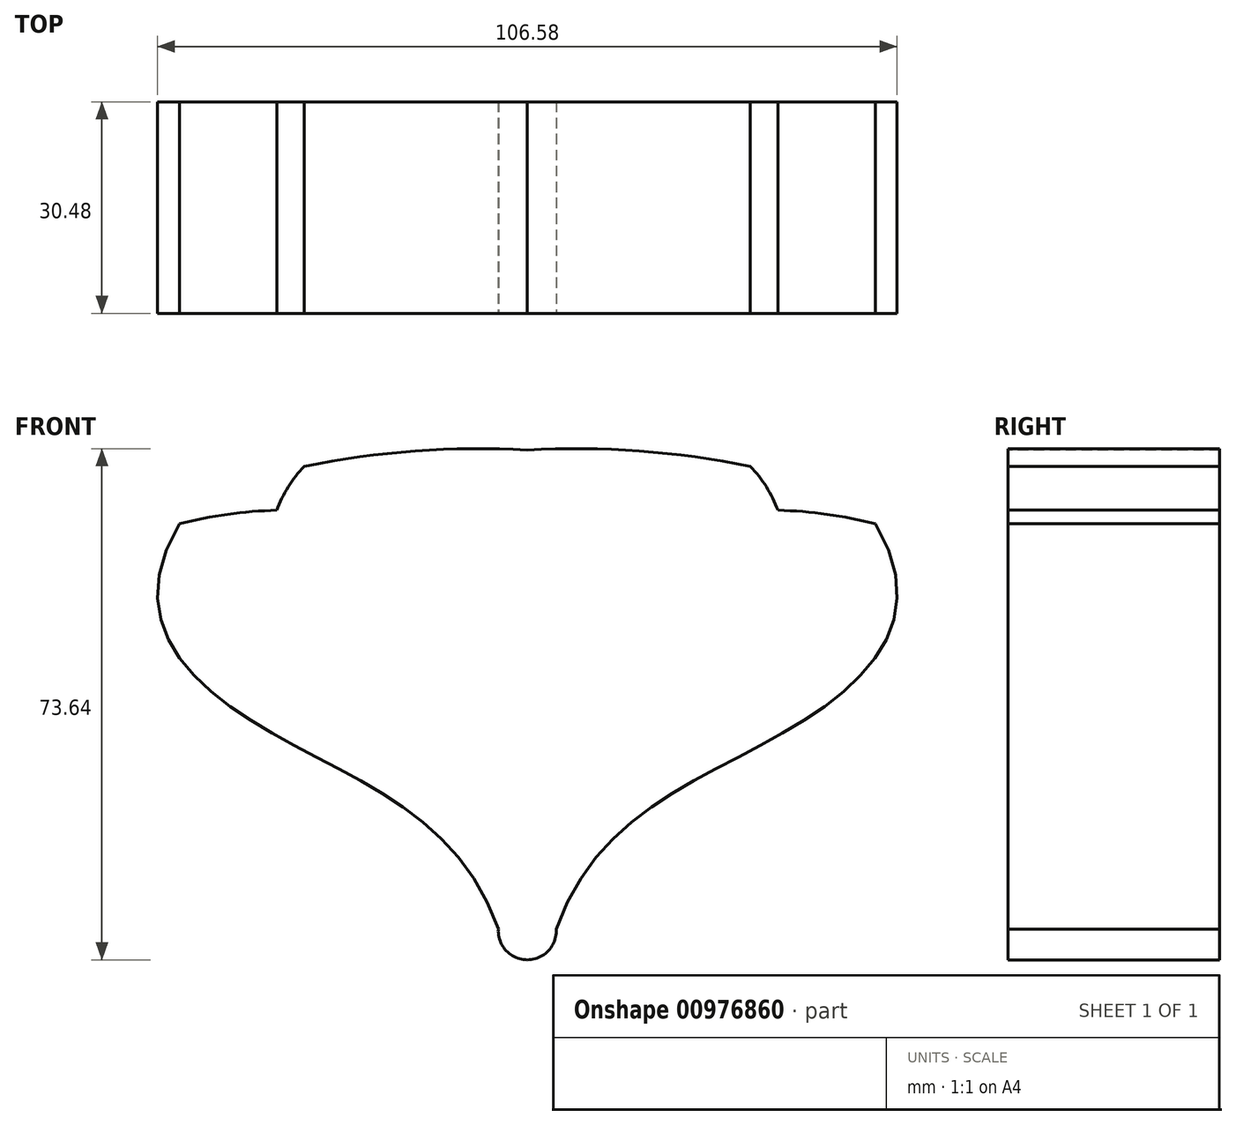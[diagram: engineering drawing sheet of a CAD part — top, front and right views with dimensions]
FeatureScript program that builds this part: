
annotation { "Feature Type Name" : "Feature", "Feature Type Description" : "" }
export const myFeature = defineFeature(function(context is Context, id is Id, definition is map)
    precondition{}
    {
        {
            var Q0;
            Q0=qCreatedBy(makeId("Front.planeOp"),FACE);
            var sketch = newSketch(context, id + "F0", { "sketchPlane" : qUnion([Q0])});
            skLineSegment(sketch, "E0.bottom", {"start": v(50.14, 29.21) * mm, "end": v(-50.14, 29.21) * mm, "construction": true});
            skLineSegment(sketch, "E0.top", {"start": v(50.14, -29.21) * mm, "end": v(-50.14, -29.21) * mm, "construction": true});
            skLineSegment(sketch, "E0.left", {"start": v(50.14, 29.21) * mm, "end": v(50.14, -29.21) * mm, "construction": true});
            skLineSegment(sketch, "E0.right", {"start": v(-50.14, 29.21) * mm, "end": v(-50.14, -29.21) * mm, "construction": true});
            skPoint(sketch, "E0.middle", {"position": v(0, 0) * mm});
            skFitSpline(sketch, "E1", {"points": [v(-50.14, 29.21) * mm, v(-38.39, 0) * mm, v(-4.18, -29.21) * mm], "startDerivative": vector(-53.87, -90.67) * mm, "endDerivative": vector(32.95, -94.62) * mm});
            skPoint(sketch, "E2", {"position": v(-50.14, 0) * mm});
            skFitSpline(sketch, "E3.MirrorCS", {"points": [v(50.14, 29.21) * mm, v(38.39, 0) * mm, v(4.18, -29.21) * mm], "startDerivative": vector(53.87, -90.67) * mm, "endDerivative": vector(-32.95, -94.62) * mm});
            skArc(sketch, "E4", {"start": v(-4.18, -29.21) * mm, "mid": v(0, -33.6) * mm, "end": v(4.18, -29.21) * mm});
            skLineSegment(sketch, "E5.bottom", {"start": v(-50.14, 29.21) * mm, "end": v(-45.63, 29.21) * mm});
            skLineSegment(sketch, "E6.bottom", {"start": v(-50.14, 29.21) * mm, "end": v(50.14, 29.21) * mm, "construction": true});
            skLineSegment(sketch, "E6.top", {"start": v(-50.14, 39.83) * mm, "end": v(50.14, 39.83) * mm, "construction": true});
            skLineSegment(sketch, "E6.left", {"start": v(-50.14, 29.21) * mm, "end": v(-50.14, 39.83) * mm, "construction": true});
            skLineSegment(sketch, "E6.right", {"start": v(50.14, 29.21) * mm, "end": v(50.14, 39.83) * mm, "construction": true});
            skArc(sketch, "E7", {"start": v(0, 39.83) * mm, "mid": v(-16.14, 39.7) * mm, "end": v(-32.13, 37.5) * mm});
            skArc(sketch, "E8", {"start": v(-32.13, 37.5) * mm, "mid": v(-34.44, 34.54) * mm, "end": v(-36.11, 31.17) * mm});
            skArc(sketch, "E9", {"start": v(-36.11, 31.17) * mm, "mid": v(-43.18, 30.6) * mm, "end": v(-50.14, 29.21) * mm});
            skArc(sketch, "E10.MirrorCS", {"start": v(0, 39.83) * mm, "mid": v(16.14, 39.7) * mm, "end": v(32.13, 37.5) * mm});
            skArc(sketch, "E11.MirrorCS", {"start": v(32.13, 37.5) * mm, "mid": v(34.44, 34.54) * mm, "end": v(36.11, 31.17) * mm});
            skArc(sketch, "E12.MirrorCS", {"start": v(36.11, 31.17) * mm, "mid": v(43.18, 30.6) * mm, "end": v(50.14, 29.21) * mm});
            skSolve(sketch);
        }
        {
            var Q0;
            Q0=sQuery(id+"F0.wireOp",EDGE,"E3.MirrorCS");
            var Q1;
            Q1=sQuery(id+"F0.wireOp",EDGE,"E12.MirrorCS");
            var Q2;
            Q2=sQuery(id+"F0.wireOp",EDGE,"E10.MirrorCS");
            var Q3;
            Q3=sQuery(id+"F0.wireOp",EDGE,"E11.MirrorCS");
            var Q4;
            Q4=sQuery(id+"F0.wireOp",EDGE,"E7");
            var Q5;
            Q5=sQuery(id+"F0.wireOp",EDGE,"E8");
            var Q6;
            Q6=sQuery(id+"F0.wireOp",EDGE,"E9");
            var Q7;
            Q7=sQuery(id+"F0.wireOp",EDGE,"E1");
            var Q8;
            Q8=sQuery(id+"F0.wireOp",EDGE,"E4");
            extrude(context, id + "F1", {"bodyType" : ToolBodyType.SURFACE, "surfaceEntities" : qUnion([Q0, Q1, Q2, Q3, Q4, Q5, Q6, Q7, Q8]), "depth" : 30.48 * mm, "offsetDistance" : 30.48 * mm});
        }
    });
